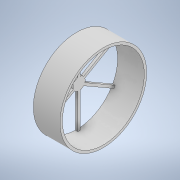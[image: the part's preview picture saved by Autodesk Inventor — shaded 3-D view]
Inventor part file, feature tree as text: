
AUTODESK INVENTOR PART (.ipt)
format: ipt  version: 2020.3 (Build 243373000, 373)  size: 157,696 bytes
history: native  units: mm
features: extrude x2, sketch x2
ambient origin geometry x8: Origin, YZ Plane, XZ Plane, XY Plane, X Axis, Y Axis, Z Axis, Center Point
bodies: Solid1 (feature_tree)
feature tree (4):
  extrude  "Extrusion1"  Depth=4.0mm
  extrude  "Extrusion2"  Depth=40.0mm
  sketch  "Sketch1"  dims[d0=135.0mm d1=4.0mm]
  sketch  "Sketch2"  dims[d2=20.0mm d3=2.0mm d4=2.0mm d5=60.0mm d7=360.0deg d9=4.0mm d10=0.0mm d11=40.0mm d12=0.0mm]
